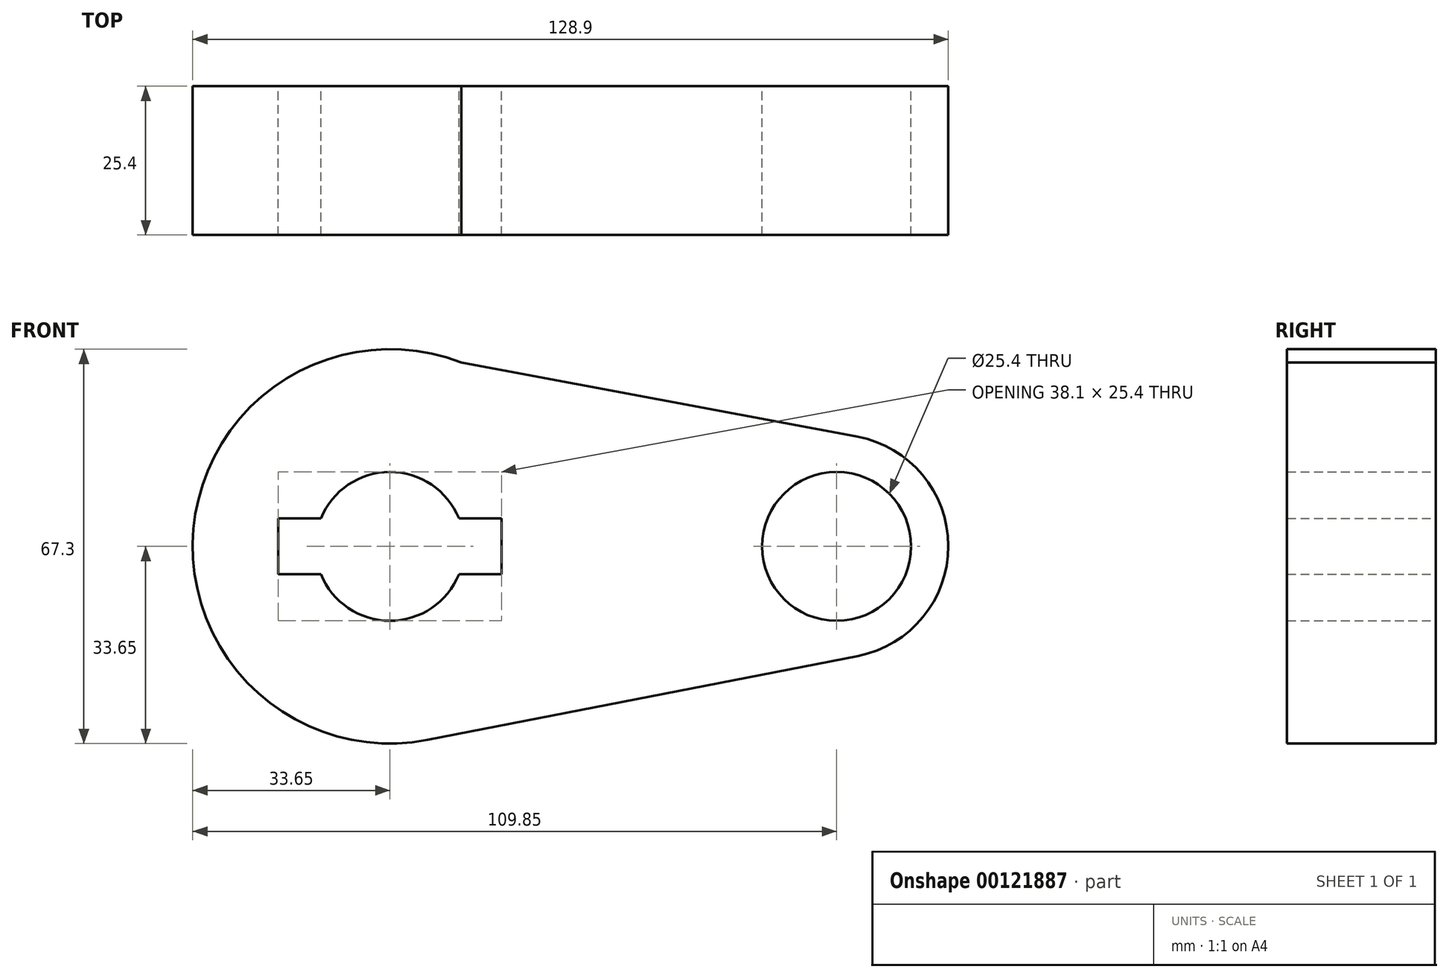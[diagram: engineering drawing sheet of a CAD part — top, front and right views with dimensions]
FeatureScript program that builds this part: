
annotation { "Feature Type Name" : "Feature", "Feature Type Description" : "" }
export const myFeature = defineFeature(function(context is Context, id is Id, definition is map)
    precondition{}
    {
        {
            var Q0;
            Q0=qCreatedBy(makeId("Front.planeOp"),FACE);
            var sketch = newSketch(context, id + "F0", { "sketchPlane" : qUnion([Q0])});
            skCircle(sketch, "E0", {"center": v(0, 0) * mm, "radius": 33.66 * mm});
            skCircle(sketch, "E1", {"center": v(76.2, 0) * mm, "radius": 19.05 * mm});
            skLineSegment(sketch, "E2", {"start": v(0, 33.66) * mm, "end": v(79.7, 18.72) * mm});
            skLineSegment(sketch, "E3", {"start": v(6.45, -33.03) * mm, "end": v(79.85, -18.7) * mm});
            skCircle(sketch, "E4", {"center": v(0, 0) * mm, "radius": 12.7 * mm});
            skCircle(sketch, "E5", {"center": v(76.2, 0) * mm, "radius": 12.7 * mm});
            skLineSegment(sketch, "E6.bottom", {"start": v(-19.05, -4.76) * mm, "end": v(19.05, -4.76) * mm});
            skLineSegment(sketch, "E6.top", {"start": v(-19.05, 4.76) * mm, "end": v(19.05, 4.76) * mm});
            skLineSegment(sketch, "E6.left", {"start": v(-19.05, -4.76) * mm, "end": v(-19.05, 4.76) * mm});
            skLineSegment(sketch, "E6.right", {"start": v(19.05, -4.76) * mm, "end": v(19.05, 4.76) * mm});
            skSolve(sketch);
        }
        {
            var Q0;
            {var subQ0=sQuery(id+"F0.wireOp",EDGE,"E6.left");Q0=makeQuery(id+"F0.imprint","IMPRINT",FACE,{"disambiguationData":[TD([[makeQuery(id+"F0.imprint","IMPRINT",EDGE,{"derivedFrom":subQ0}),1.0]])]});}
            extrude(context, id + "F1", {"entities" : qUnion([Q0]), "depth" : 25.4 * mm});
        }
        {
            var Q0;
            Q0 = qSketchRegion(id + "F0", true);
            extrude(context, id + "F2", {"entities" : qUnion([Q0]), "operationType" : NewBodyOperationType.ADD, "depth" : 25.4 * mm});
        }
        {
            var Q0;
            Q0=sQuery(id+"F0.wireOp",EDGE,"E0");
            var Q1;
            Q1=sQuery(id+"F0.wireOp",EDGE,"E5");
            extrude(context, id + "F3", {"bodyType" : ToolBodyType.SURFACE, "surfaceEntities" : qUnion([Q0, Q1]), "endBound" : BoundingType.SYMMETRIC, "depth" : 25.4 * mm});
        }
    });
